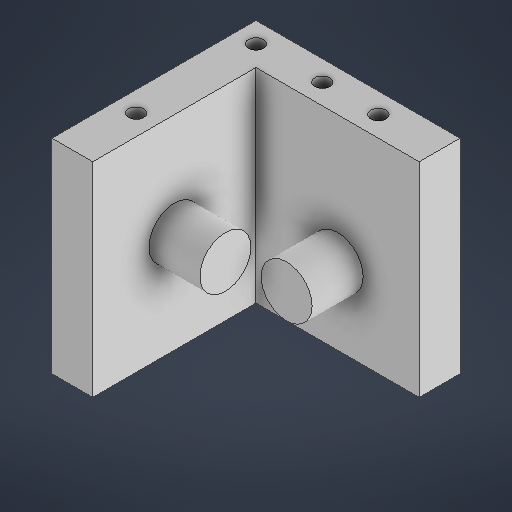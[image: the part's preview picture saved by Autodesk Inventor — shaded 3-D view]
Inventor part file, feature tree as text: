
AUTODESK INVENTOR PART (.ipt)
format: ipt  version: 2025 (Build 290162000, 162)  size: 225,792 bytes
history: native  units: in
note: dims shown in document units (in); Inventor stores cm internally (conversion verified against a paired STEP export)
features: sketch x4, extrude x3, hole x1
ambient origin geometry x8: Origin, YZ Plane, XZ Plane, XY Plane, X Axis, Y Axis, Z Axis, Center Point
bodies: Solid1 (feature_tree)
feature tree (8):
  extrude  "Extrusion1"  Depth=0.315in
  hole  "Hole1"  [1 undecoded]
  extrude  "Extrusion2"  Depth=0.1969in
  extrude  "Extrusion3"  Depth=0.1969in
  sketch  "Sketch1"  dims[d0=1.5748in d1=0.315in]
  sketch  "Sketch2"  dims[d2=0.315in d3=1.5748in]
  sketch  "Sketch3"  dims[d4=1.5748in d5=0.0in d6=0.1969in]
  sketch  "Sketch4"  dims[d7=0.1969in d8=0.1969in d9=0.1969in d10=0.4724in d11=0.4331in d14=0.1181in d15=0.2362in d16=0.1575in d17=0.0787in d18=90.0deg d19=0.4331in d20=0.8108in d21=0.4921in d22=0.9055in d23=0.3937in d24=0.3937in d25=0.0in d26=0.3937in d27=0.5906in d28=0.6299in d29=0.3937in d30=0.0in d31=0.6299in]
note: 1 required parameter value undecoded (feature->parameter linkage not recoverable at this tier; creation-order binding heuristic only, values carry confidence <= 0.55)
